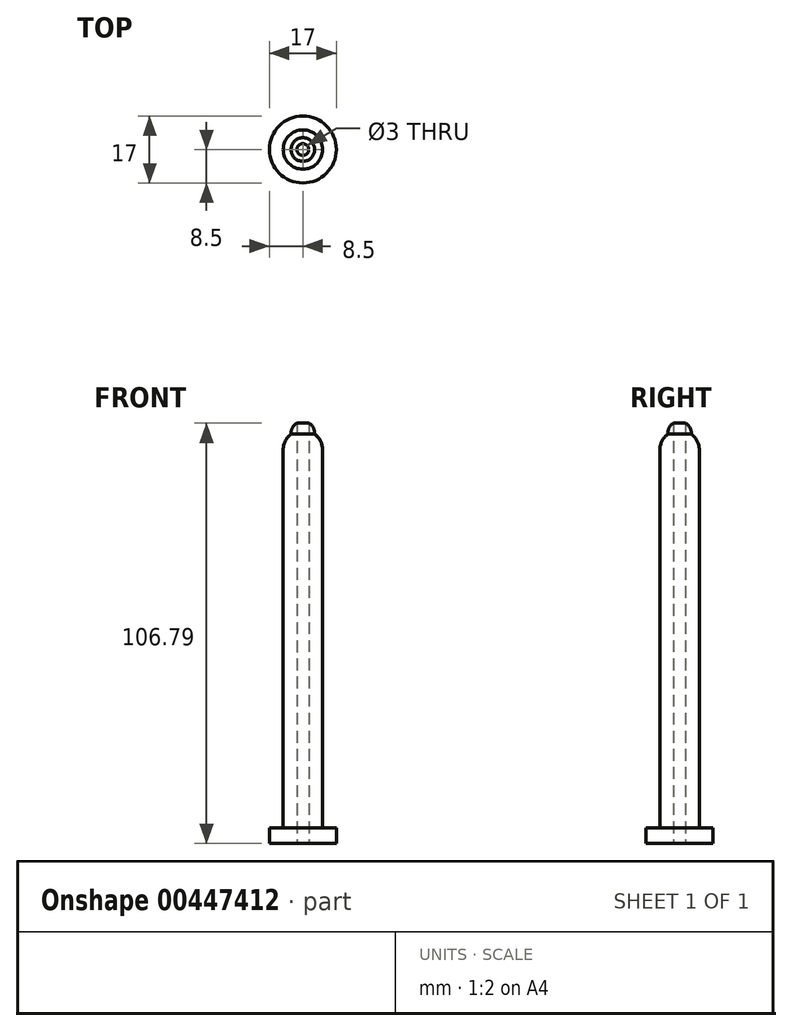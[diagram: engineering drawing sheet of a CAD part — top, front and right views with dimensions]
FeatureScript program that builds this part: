
annotation { "Feature Type Name" : "Feature", "Feature Type Description" : "" }
export const myFeature = defineFeature(function(context is Context, id is Id, definition is map)
    precondition{}
    {
        {
            var Q0;
            Q0=qCreatedBy(makeId("Top.planeOp"),FACE);
            var sketch = newSketch(context, id + "F0", { "sketchPlane" : qUnion([Q0])});
            skCircle(sketch, "E0", {"center": v(0, 0) * mm, "radius": 8.5 * mm});
            skSolve(sketch);
        }
        {
            var Q0;
            Q0=qSketchRegion(id+"F0",true);
            extrude(context, id + "F1", {"entities" : qUnion([Q0]), "depth" : 4 * mm});
        }
        {
            var Q0;
            Q0=qCreatedBy(makeId("Top.planeOp"),FACE);
            var sketch = newSketch(context, id + "F2", { "sketchPlane" : qUnion([Q0])});
            skCircle(sketch, "E1", {"center": v(0, 0) * mm, "radius": 5 * mm});
            skSolve(sketch);
        }
        {
            var Q0;
            Q0=qSketchRegion(id+"F2",true);
            extrude(context, id + "F3", {"entities" : qUnion([Q0]), "operationType" : NewBodyOperationType.ADD, "depth" : 100 * mm});
        }
        {
            var Q0;
            Q0=qCreatedBy(makeId("Right.planeOp"),FACE);
            var sketch = newSketch(context, id + "F4", { "sketchPlane" : qUnion([Q0])});
            skLineSegment(sketch, "E2", {"start": v(0, 100) * mm, "end": v(5, 100) * mm});
            skArc(sketch, "E3", {"start": v(5, 100) * mm, "mid": v(3.54, 103.54) * mm, "end": v(0, 105) * mm});
            skLineSegment(sketch, "E4", {"start": v(3, 104) * mm, "end": v(0, 104) * mm});
            skArc(sketch, "E5", {"start": v(3, 104) * mm, "mid": v(2.19, 106.24) * mm, "end": v(0, 107.19) * mm});
            skLineSegment(sketch, "E6", {"start": v(0, 107.19) * mm, "end": v(0, 100) * mm});
            skSolve(sketch);
        }
        {
            var Q0;
            {var subQ0=sQuery(id+"F4.wireOp",EDGE,"E2");Q0=makeQuery(id+"F4.imprint","IMPRINT",FACE,{"disambiguationData":[TD([[makeQuery(id+"F4.imprint","IMPRINT",EDGE,{"derivedFrom":subQ0}),1.0]])]});}
            var Q1;
            {var subQ3=sQuery(id+"F4.wireOp",EDGE,"E5");Q1=makeQuery(id+"F4.imprint","IMPRINT",FACE,{"disambiguationData":[TD([[makeQuery(id+"F4.imprint","IMPRINT",EDGE,{"derivedFrom":subQ3}),1.0]])]});}
            var Q2;
            {var subQ0=sQuery(id+"F4.wireOp",EDGE,"E6");var subQ1=sQuery(id+"F4.wireOp",EDGE,"E3");var subQ2=makeQuery(id+"F4.imprint","INTERSECT",VERTEX,{"derivedFrom":[subQ1,subQ0]});Q2=makeQuery(id+"F4.imprint","IMPRINT",FACE,{"disambiguationData":[TD([[makeQuery(id+"F4.imprint","IMPRINT",EDGE,{"disambiguationData":[TD([[subQ2,-1.0]])],"derivedFrom":subQ0}),1.0]])]});}
            var Q3;
            Q3=sQuery(id+"F4.wireOp",EDGE,"E6");
            revolve(context, id + "F5", {"operationType" : NewBodyOperationType.ADD, "entities" : qUnion([Q0, Q1, Q2]), "axis" : qUnion([Q3]), "revolveType" : RevolveType.FULL});
        }
        {
            var Q0;
            Q0=makeQuery(id+"F1.opExtrude","CAP_FACE",FACE,{"disambiguationData":[OSD([sQuery(id+"F0.wireOp",EDGE,"E0")])],"isStart":true});
            var sketch = newSketch(context, id + "F6", { "sketchPlane" : qUnion([Q0])});
            skCircle(sketch, "E7", {"center": v(0, 0) * mm, "radius": 1.5 * mm});
            skSolve(sketch);
        }
        {
            var Q0;
            Q0 = qSketchRegion(id + "F6", true);
            extrude(context, id + "F7", {"entities" : qUnion([Q0]), "operationType" : NewBodyOperationType.REMOVE, "oppositeDirection" : true, "depth" : 121.2 * mm});
        }
    });
